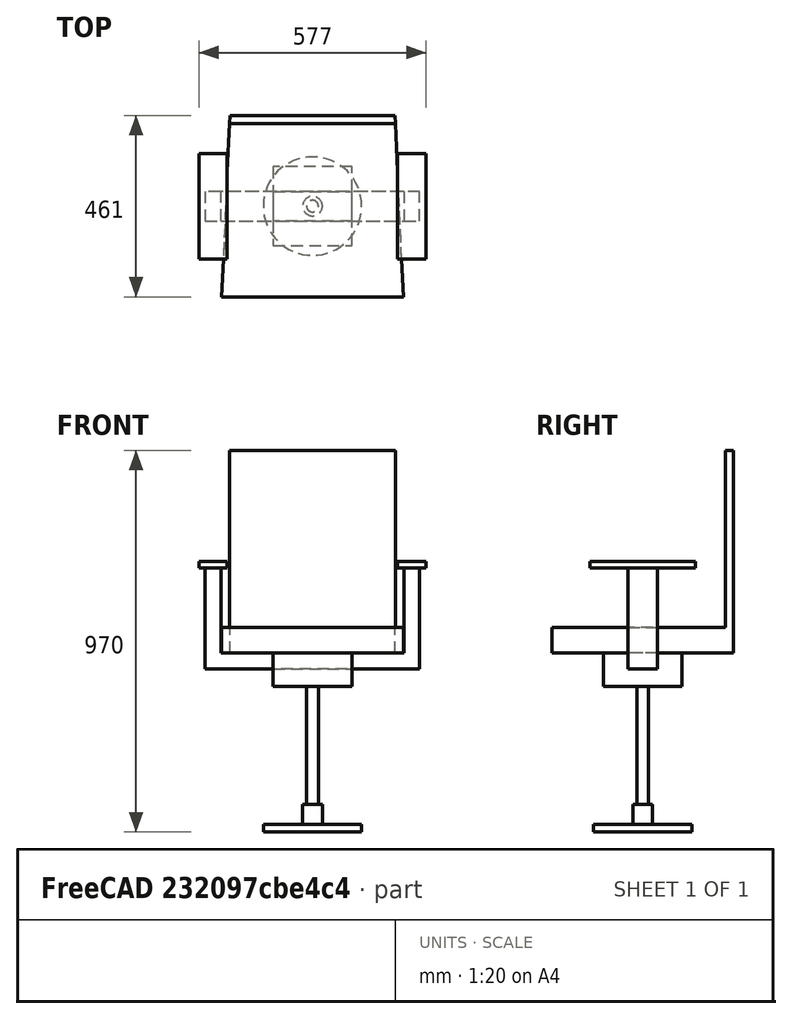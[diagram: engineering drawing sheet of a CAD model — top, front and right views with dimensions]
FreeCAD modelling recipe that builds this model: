
FCSTD DOCUMENT  (FreeCAD 1.0R39109 (Git))
Label: chair02_00504
License: All rights reserved
LicenseURL: https://en.wikipedia.org/wiki/All_rights_reserved
objects: TechDraw::DrawViewDimension×17, Sketcher::SketchObject×10, PartDesign::Pad×10, TechDraw::DrawViewAnnotation×9, PartDesign::Body×5, PartDesign::ShapeBinder×4, TechDraw::DrawSVGTemplate×3, TechDraw::DrawProjGroupItem×3, TechDraw::DrawPage×3, TechDraw::DrawViewSection×3, App::Part×1
note: 90 computed .brp shape members not serialized (recipe doc carries the construction recipe); baked Part::Feature solids carry a one-line shape summary decoded from their .brp

FEATURE [Sketcher::SketchObject] Sketch
  ArcFitTolerance = 1e-06
  AttachmentSupport = -> [XY_Plane]
  FullyConstrained = true
  MakeInternals = false
  MapMode = 5
  sketch-geometry (1):
    g0: Circle CenterX=0 CenterY=0 CenterZ=0 NormalX=0 NormalY=0 NormalZ=1 AngleXU=0 Radius=125
  constraints (2):
    c: Diameter(g0) = 250
    c: Coincident(g0,g-1)
FEATURE [PartDesign::Pad] Pad
  Direction = (0,0,1)
  Length = 20
  Length2 = 10
  Profile = -> Sketch
  ReferenceAxis = -> Sketch [N_Axis]
  Refine = true
  Suppressed = false
  Type = 0
FEATURE [Sketcher::SketchObject] Sketch001
  ArcFitTolerance = 1e-06
  AttachmentSupport = -> [Pad]
  FullyConstrained = true
  MakeInternals = false
  MapMode = 5
  Placement = pos=(0,0,20) rot=(0,0,1;0rad)
  sketch-geometry (1):
    g0: Circle CenterX=0 CenterY=0 CenterZ=0 NormalX=0 NormalY=0 NormalZ=1 AngleXU=0 Radius=25
  constraints (2):
    c: Diameter(g0) = 50
    c: Coincident(g0,g-1)
FEATURE [PartDesign::Pad] Pad001
  BaseFeature = -> Pad
  Direction = (0,0,1)
  Length = 50
  Length2 = 10
  Profile = -> Sketch001
  ReferenceAxis = -> Sketch001 [N_Axis]
  Refine = true
  Suppressed = false
  Type = 0
FEATURE [PartDesign::Body] Body  label="Body1"
  AllowCompound = false
  Group = -> [Sketch,Pad,Sketch001,Pad001]
  Origin = -> Origin
  Tip = -> Pad001
FEATURE [PartDesign::ShapeBinder] CopyPad001  label="Body2_Sketch_P.lane"
  Placement = pos=(0,0,50) rot=(0,0,1;0rad)
  TraceSupport = false
FEATURE [Sketcher::SketchObject] Sketch002
  ArcFitTolerance = 1e-06
  AttachmentSupport = -> [CopyPad001]
  FullyConstrained = true
  MakeInternals = false
  MapMode = 5
  Placement = pos=(0,0,70) rot=(0,0,1;0rad)
  sketch-geometry (1):
    g0: Circle CenterX=0 CenterY=0 CenterZ=0 NormalX=0 NormalY=0 NormalZ=1 AngleXU=0 Radius=15
  constraints (2):
    c: Diameter(g0) = 30
    c: Coincident(g0,g-1)
FEATURE [PartDesign::Pad] Pad002
  Direction = (0,0,1)
  Length = 300
  Length2 = 10
  Placement = pos=(0,0,50) rot=(0,0,1;0rad)
  Profile = -> Sketch002
  ReferenceAxis = -> Sketch002 [N_Axis]
  Refine = true
  Suppressed = false
  Type = 0
FEATURE [PartDesign::Body] Body001  label="Body2"
  AllowCompound = false
  Group = -> [CopyPad001,Sketch002,Pad002]
  Origin = -> Origin001
  Tip = -> Pad002
FEATURE [PartDesign::ShapeBinder] CopyPad002  label="Body3_Sketch_Plane"
  Placement = pos=(0,0,300) rot=(0,0,1;0rad)
  TraceSupport = false
FEATURE [Sketcher::SketchObject] Sketch003
  ArcFitTolerance = 1e-06
  AttachmentSupport = -> [CopyPad002]
  FullyConstrained = true
  MakeInternals = false
  MapMode = 5
  Placement = pos=(0,0,370) rot=(0,0,1;0rad)
  sketch-geometry (5):
    g0: LineSegment StartX=-100 StartY=-100 StartZ=0 EndX=100 EndY=-100 EndZ=0
    g1: LineSegment StartX=100 StartY=-100 StartZ=0 EndX=100 EndY=100 EndZ=0
    g2: LineSegment StartX=100 StartY=100 StartZ=0 EndX=-100 EndY=100 EndZ=0
    g3: LineSegment StartX=-100 StartY=100 StartZ=0 EndX=-100 EndY=-100 EndZ=0
    g4: GeomPoint [constr] X=0 Y=0 Z=0
  constraints (12):
    c: Coincident(g0,g1)
    c: Coincident(g1,g2)
    c: Coincident(g2,g3)
    c: Coincident(g3,g0)
    c: Horizontal(g0)
    c: Horizontal(g2)
    c: Vertical(g1)
    c: Vertical(g3)
    c: Symmetric(g2,g0,g4)
    c: Distance(g1,g3) = 200
    c: Distance(g0,g2) = 200
    c: Coincident(g4,g-1)
FEATURE [PartDesign::Pad] Pad003
  Direction = (0,0,1)
  Length = 45
  Length2 = 10
  Placement = pos=(0,0,300) rot=(0,0,1;0rad)
  Profile = -> Sketch003
  ReferenceAxis = -> Sketch003 [N_Axis]
  Refine = true
  Suppressed = false
  Type = 0
FEATURE [PartDesign::ShapeBinder] CopyPad003  label="Body4_Sketch_Plane"
  Placement = pos=(0,0,45) rot=(0,0,1;0rad)
  TraceSupport = false
FEATURE [Sketcher::SketchObject] Sketch004
  ArcFitTolerance = 1e-06
  AttachmentSupport = -> [CopyPad003]
  FullyConstrained = true
  MakeInternals = false
  MapMode = 5
  Placement = pos=(0,0,415) rot=(0,0,1;0rad)
  sketch-geometry (5):
    g0: LineSegment StartX=-272.5 StartY=-37.5 StartZ=0 EndX=272.5 EndY=-37.5 EndZ=0
    g1: LineSegment StartX=272.5 StartY=-37.5 StartZ=0 EndX=272.5 EndY=37.5 EndZ=0
    g2: LineSegment StartX=272.5 StartY=37.5 StartZ=0 EndX=-272.5 EndY=37.5 EndZ=0
    g3: LineSegment StartX=-272.5 StartY=37.5 StartZ=0 EndX=-272.5 EndY=-37.5 EndZ=0
    g4: GeomPoint [constr] X=0 Y=0 Z=0
  constraints (12):
    c: Coincident(g0,g1)
    c: Coincident(g1,g2)
    c: Coincident(g2,g3)
    c: Coincident(g3,g0)
    c: Horizontal(g0)
    c: Horizontal(g2)
    c: Vertical(g1)
    c: Vertical(g3)
    c: Symmetric(g2,g0,g4)
    c: Distance(g1,g3) = 545
    c: Distance(g0,g2) = 75
    c: Coincident(g4,g-1)
FEATURE [PartDesign::Pad] Pad004
  Direction = (0,0,1)
  Length = 40
  Length2 = 10
  Placement = pos=(0,0,45) rot=(0,0,1;0rad)
  Profile = -> Sketch004
  ReferenceAxis = -> Sketch004 [N_Axis]
  Refine = true
  Suppressed = false
  Type = 0
FEATURE [Sketcher::SketchObject] Sketch005
  ArcFitTolerance = 1e-06
  AttachmentSupport = -> [Pad004]
  ExternalGeometry = -> [Pad004]
  FullyConstrained = true
  MakeInternals = false
  MapMode = 5
  Placement = pos=(0,0,455) rot=(0,0,1;0rad)
  sketch-geometry (8):
    g0: LineSegment StartX=-272.5 StartY=37.5 StartZ=0 EndX=-272.5 EndY=-37.5 EndZ=0
    g1: LineSegment StartX=-272.5 StartY=-37.5 StartZ=0 EndX=-232.5 EndY=-37.5 EndZ=0
    g2: LineSegment StartX=-232.5 StartY=-37.5 StartZ=0 EndX=-232.5 EndY=37.5 EndZ=0
    g3: LineSegment StartX=-232.5 StartY=37.5 StartZ=0 EndX=-272.5 EndY=37.5 EndZ=0
    g4: LineSegment StartX=272.5 StartY=37.5 StartZ=0 EndX=232.5 EndY=37.5 EndZ=0
    g5: LineSegment StartX=232.5 StartY=37.5 StartZ=0 EndX=232.5 EndY=-37.5 EndZ=0
    g6: LineSegment StartX=232.5 StartY=-37.5 StartZ=0 EndX=272.5 EndY=-37.5 EndZ=0
    g7: LineSegment StartX=272.5 StartY=-37.5 StartZ=0 EndX=272.5 EndY=37.5 EndZ=0
  constraints (22):
    c: Coincident(g0,g1)
    c: Coincident(g1,g2)
    c: Coincident(g2,g3)
    c: Coincident(g3,g0)
    c: Vertical(g0)
    c: Vertical(g2)
    c: Horizontal(g1)
    c: Horizontal(g3)
    c: Coincident(g0,g-3)
    c: PointOnObject(g1,g-4)
    c: DistanceX(g3,g3) = 40
    c: Coincident(g4,g5)
    c: Coincident(g5,g6)
    c: Coincident(g6,g7)
    c: Coincident(g7,g4)
    c: Horizontal(g4)
    c: Horizontal(g6)
    c: Vertical(g5)
    c: Vertical(g7)
    c: Coincident(g4,g-3)
    c: PointOnObject(g5,g-4)
    c: Equal(g4,g3)
FEATURE [PartDesign::Pad] Pad005
  BaseFeature = -> Pad004
  Direction = (0,0,1)
  Length = 216
  Length2 = 10
  Placement = pos=(0,0,45) rot=(0,0,1;0rad)
  Profile = -> Sketch005
  ReferenceAxis = -> Sketch005 [N_Axis]
  Refine = true
  Suppressed = false
  Type = 0
FEATURE [Sketcher::SketchObject] Sketch006
  ArcFitTolerance = 1e-06
  AttachmentSupport = -> [Pad005]
  ExternalGeometry = -> [Pad005]
  FullyConstrained = true
  MakeInternals = false
  MapMode = 5
  Placement = pos=(0,0,671) rot=(0,0,1;0rad)
  sketch-geometry (16):
    g0: LineSegment StartX=-288.5 StartY=134 StartZ=0 EndX=-288.5 EndY=-134 EndZ=0
    g1: LineSegment StartX=-288.5 StartY=-134 StartZ=0 EndX=-216.5 EndY=-134 EndZ=0
    g2: LineSegment StartX=-216.5 StartY=-134 StartZ=0 EndX=-216.5 EndY=134 EndZ=0
    g3: LineSegment StartX=-216.5 StartY=134 StartZ=0 EndX=-288.5 EndY=134 EndZ=0
    g4: LineSegment StartX=216.5 StartY=134 StartZ=0 EndX=216.5 EndY=-134 EndZ=0
    g5: LineSegment StartX=216.5 StartY=-134 StartZ=0 EndX=288.5 EndY=-134 EndZ=0
    g6: LineSegment StartX=288.5 StartY=-134 StartZ=0 EndX=288.5 EndY=134 EndZ=0
    g7: LineSegment StartX=288.5 StartY=134 StartZ=0 EndX=216.5 EndY=134 EndZ=0
    g8: LineSegment [constr] StartX=-272.5 StartY=37.5 StartZ=0 EndX=-232.5 EndY=-37.5 EndZ=0
    g9: LineSegment [constr] StartX=-252.5 StartY=0 StartZ=0 EndX=-272.5 EndY=-37.5 EndZ=0
    g10: LineSegment [constr] StartX=232.5 StartY=37.5 StartZ=0 EndX=272.5 EndY=-37.5 EndZ=0
    g11: LineSegment [constr] StartX=272.5 StartY=37.5 StartZ=0 EndX=252.5 EndY=0 EndZ=0
    g12: LineSegment [constr] StartX=-216.5 StartY=134 StartZ=0 EndX=-288.5 EndY=-134 EndZ=0
    g13: LineSegment [constr] StartX=-288.5 StartY=134 StartZ=0 EndX=-252.5 EndY=0 EndZ=0
    g14: LineSegment [constr] StartX=216.5 StartY=134 StartZ=0 EndX=288.5 EndY=-134 EndZ=0
    g15: LineSegment [constr] StartX=288.5 StartY=134 StartZ=0 EndX=252.5 EndY=0 EndZ=0
  constraints (38):
    c: Coincident(g0,g1)
    c: Coincident(g1,g2)
    c: Coincident(g2,g3)
    c: Coincident(g3,g0)
    c: Vertical(g0)
    c: Vertical(g2)
    c: Horizontal(g1)
    c: Horizontal(g3)
    c: Coincident(g4,g5)
    c: Coincident(g5,g6)
    c: Coincident(g6,g7)
    c: Coincident(g7,g4)
    c: Vertical(g4)
    c: Vertical(g6)
    c: Horizontal(g5)
    c: Horizontal(g7)
    c: Equal(g7,g3)
    c: Equal(g2,g4)
    c: DistanceX(g3,g3) = 72
    c: Coincident(g8,g-4)
    c: Coincident(g8,g-3)
    c: Coincident(g9,g-4)
    c: Coincident(g10,g-5)
    c: Coincident(g10,g-6)
    c: Coincident(g11,g-6)
    c: Symmetric(g10,g10,g11)
    c: Symmetric(g8,g8,g9)
    c: Coincident(g12,g2)
    c: Coincident(g12,g0)
    c: Coincident(g13,g0)
    c: Symmetric(g12,g12,g13)
    c: Coincident(g9,g13)
    c: Coincident(g14,g4)
    c: Coincident(g14,g5)
    c: Coincident(g15,g6)
    c: Symmetric(g14,g14,g15)
    c: Coincident(g15,g11)
    c: DistanceY(g2,g2) = 268
FEATURE [PartDesign::Pad] Pad006
  BaseFeature = -> Pad005
  Direction = (0,0,1)
  Length = 17
  Length2 = 10
  Placement = pos=(0,0,45) rot=(0,0,1;0rad)
  Profile = -> Sketch006
  ReferenceAxis = -> Sketch006 [N_Axis]
  Refine = true
  Suppressed = false
  Type = 0
FEATURE [PartDesign::Body] Body003  label="Body4"
  AllowCompound = false
  Group = -> [CopyPad003,Sketch004,Pad004,Sketch005,Pad005,Sketch006,Pad006]
  Origin = -> Origin003
  Tip = -> Pad006
FEATURE [PartDesign::ShapeBinder] CopyPad006  label="Body5_Sketch_Plane"
  Placement = pos=(0,0,45) rot=(0,0,1;0rad)
  TraceSupport = false
FEATURE [Sketcher::SketchObject] Sketch009
  ArcFitTolerance = 1e-06
  AttachmentSupport = -> [Pad003]
  ExternalGeometry = -> [Pad003]
  FullyConstrained = true
  MakeInternals = false
  MapMode = 5
  Placement = pos=(0,0,415) rot=(0,0,1;0rad)
  sketch-geometry (8):
    g0: LineSegment StartX=-100 StartY=100 StartZ=0 EndX=-100 EndY=37.5 EndZ=0
    g1: LineSegment StartX=-100 StartY=37.5 StartZ=0 EndX=100 EndY=37.5 EndZ=0
    g2: LineSegment StartX=100 StartY=37.5 StartZ=0 EndX=100 EndY=100 EndZ=0
    g3: LineSegment StartX=100 StartY=100 StartZ=0 EndX=-100 EndY=100 EndZ=0
    g4: LineSegment StartX=100 StartY=-100 StartZ=0 EndX=100 EndY=-37.5 EndZ=0
    g5: LineSegment StartX=100 StartY=-37.5 StartZ=0 EndX=-100 EndY=-37.5 EndZ=0
    g6: LineSegment StartX=-100 StartY=-37.5 StartZ=0 EndX=-100 EndY=-100 EndZ=0
    g7: LineSegment StartX=-100 StartY=-100 StartZ=0 EndX=100 EndY=-100 EndZ=0
  constraints (21):
    c: Coincident(g0,g1)
    c: Coincident(g1,g2)
    c: Coincident(g2,g3)
    c: Coincident(g3,g0)
    c: Vertical(g0)
    c: Vertical(g2)
    c: Horizontal(g1)
    c: Horizontal(g3)
    c: Coincident(g0,g-3)
    c: PointOnObject(g1,g-4)
    c: Coincident(g4,g5)
    c: Coincident(g5,g6)
    c: Coincident(g6,g7)
    c: Coincident(g7,g4)
    c: Vertical(g6)
    c: Horizontal(g5)
    c: Horizontal(g7)
    c: Coincident(g4,g-4)
    c: PointOnObject(g5,g-3)
    c: DistanceY(g4,g1) = 75
    c: Symmetric(g1,g4,g-1)
FEATURE [PartDesign::Pad] Pad009
  BaseFeature = -> Pad003
  Direction = (0,0,1)
  Length = 40
  Length2 = 10
  Placement = pos=(0,0,300) rot=(0,0,1;0rad)
  Profile = -> Sketch009
  ReferenceAxis = -> Sketch009 [N_Axis]
  Refine = true
  Suppressed = false
  Type = 0
FEATURE [PartDesign::Body] Body002  label="Body3"
  AllowCompound = false
  Group = -> [CopyPad002,Sketch003,Pad003,Sketch009,Pad009]
  Origin = -> Origin002
  Tip = -> Pad009
FEATURE [Sketcher::SketchObject] Sketch007
  ArcFitTolerance = 1e-06
  AttachmentSupport = -> [CopyPad006]
  FullyConstrained = true
  MakeInternals = false
  MapMode = 5
  Placement = pos=(0,0,455) rot=(0,0,1;0rad)
  sketch-geometry (8):
    g0: LineSegment StartX=-210 StartY=230.5 StartZ=0 EndX=-231 EndY=-230.5 EndZ=0
    g1: LineSegment StartX=-231 StartY=-230.5 StartZ=0 EndX=231 EndY=-230.5 EndZ=0
    g2: LineSegment StartX=231 StartY=-230.5 StartZ=0 EndX=210 EndY=230.5 EndZ=0
    g3: LineSegment StartX=210 StartY=230.5 StartZ=0 EndX=-210 EndY=230.5 EndZ=0
    g4: LineSegment [constr] StartX=210 StartY=230.5 StartZ=0 EndX=2.84e-14 EndY=0 EndZ=0
    g5: LineSegment [constr] StartX=2.84e-14 StartY=0 StartZ=0 EndX=-210 EndY=230.5 EndZ=0
    g6: LineSegment [constr] StartX=210 StartY=230.5 StartZ=0 EndX=210 EndY=0 EndZ=0
    g7: LineSegment [constr] StartX=231 StartY=-230.5 StartZ=0 EndX=231 EndY=0 EndZ=0
  constraints (20):
    c: Coincident(g2,g1)
    c: DistanceX(g1,g1) = 462
    c: DistanceX(g3,g3) = 420
    c: Coincident(g1,g0)
    c: Symmetric(g2,g0,g-2)
    c: Coincident(g2,g3)
    c: Coincident(g3,g0)
    c: Coincident(g4,g2)
    c: Coincident(g4,g-1)
    c: Coincident(g5,g4)
    c: Coincident(g5,g0)
    c: DistanceY(g2,g2) = 461
    c: Coincident(g6,g2)
    c: PointOnObject(g6,g-1)
    c: Vertical(g6)
    c: Coincident(g7,g1)
    c: PointOnObject(g7,g-1)
    c: Vertical(g7)
    c: Equal(g7,g6)
    c: Symmetric(g1,g0,g-2)
FEATURE [PartDesign::Pad] Pad007
  Direction = (0,0,1)
  Length = 65
  Length2 = 10
  Placement = pos=(0,0,45) rot=(0,0,1;0rad)
  Profile = -> Sketch007
  ReferenceAxis = -> Sketch007 [N_Axis]
  Refine = true
  Suppressed = false
  Type = 0
FEATURE [Sketcher::SketchObject] Sketch008
  ArcFitTolerance = 1e-06
  AttachmentSupport = -> [Pad007]
  ExternalGeometry = -> [Pad007]
  FullyConstrained = true
  MakeInternals = false
  MapMode = 5
  Placement = pos=(0,0,520) rot=(0,0,1;0rad)
  sketch-geometry (4):
    g0: LineSegment StartX=-210 StartY=230.5 StartZ=0 EndX=210 EndY=230.5 EndZ=0
    g1: LineSegment StartX=-210 StartY=230.5 StartZ=0 EndX=-210.957 EndY=209.5 EndZ=0
    g2: LineSegment StartX=-210.957 StartY=209.5 StartZ=0 EndX=210.957 EndY=209.5 EndZ=0
    g3: LineSegment StartX=210 StartY=230.5 StartZ=0 EndX=210.957 EndY=209.5 EndZ=0
  constraints (10):
    c: Coincident(g0,g-3)
    c: Coincident(g0,g-4)
    c: Coincident(g1,g0)
    c: PointOnObject(g1,g-3)
    c: Coincident(g2,g1)
    c: PointOnObject(g2,g-4)
    c: Horizontal(g2)
    c: Coincident(g3,g0)
    c: Coincident(g3,g2)
    c: DistanceY(g1,g1) = 21
FEATURE [PartDesign::Pad] Pad008
  BaseFeature = -> Pad007
  Direction = (0,0,1)
  Length = 450
  Length2 = 10
  Placement = pos=(0,0,45) rot=(0,0,1;0rad)
  Profile = -> Sketch008
  ReferenceAxis = -> Sketch008 [N_Axis]
  Refine = true
  Suppressed = false
  Type = 0
FEATURE [PartDesign::Body] Body004  label="Body5"
  AllowCompound = false
  Group = -> [CopyPad006,Sketch007,Pad007,Sketch008,Pad008]
  Origin = -> Origin004
  Tip = -> Pad008
FEATURE [App::Part] Part  label="chair02"
  Group = -> [Body,Body001,Body002,Body003,Body004]
  Origin = -> Origin005
FEATURE [TechDraw::DrawSVGTemplate] Template  label="テンプレート"
  Height = 210
  Orientation = 1
  Template = <userpath>/AppData/Local/Programs/FreeCAD 1.0/data/Mod/TechDraw/Templates/A4_Landscape_blank.svg
  Width = 297
FEATURE [TechDraw::DrawProjGroupItem] View
  CoarseView = false
  Direction = (0,0,1)
  Focus = 100
  HardHidden = true
  IsoCount = 0
  IsoHidden = false
  IsoVisible = false
  LockPosition = false
  Perspective = false
  Rotation = 0
  RotationVector = (1,0,0)
  Scale = 0.333333
  ScaleType = 2
  ScrubCount = 1
  SeamHidden = false
  SeamVisible = false
  SmoothHidden = false
  SmoothVisible = true
  Source = -> [Part]
  Type = 0
  X = 131.425
  XDirection = (1,0,0)
  Y = 107.897
FEATURE [TechDraw::DrawViewDimension] Dimension  label="寸法"
  AngleOverride = false
  Arbitrary = false
  ArbitraryTolerances = false
  BoxCorners = (2) [(-96.1666,-76.8333,0),(96.1666,76.8333,0)]
  EqualTolerance = true
  ExtensionAngle = 0
  FormatSpec = %.2w
  FormatSpecOverTolerance = %+.2w
  FormatSpecUnderTolerance = %+.2w
  Inverted = false
  LineAngle = 0
  LockPosition = false
  MeasureType = 1
  OverTolerance = 0
  References2D = -> [View]
  Rotation = 0
  Scale = 0.2
  ScaleType = 2
  TheoreticalExact = false
  Type = 1
  UnderTolerance = 0
  X = 0
  Y = 93.9298
FEATURE [TechDraw::DrawViewDimension] Dimension001  label="寸法001"
  AngleOverride = false
  Arbitrary = false
  ArbitraryTolerances = false
  BoxCorners = (2) [(-96.1666,-76.8333,0),(96.1666,76.8333,0)]
  EqualTolerance = true
  ExtensionAngle = 0
  FormatSpec = %.2w
  FormatSpecOverTolerance = %+.2w
  FormatSpecUnderTolerance = %+.2w
  Inverted = false
  LineAngle = 0
  LockPosition = false
  MeasureType = 1
  OverTolerance = 0
  References2D = -> [View]
  Rotation = 0
  Scale = 0.2
  ScaleType = 2
  TheoreticalExact = false
  Type = 2
  UnderTolerance = 0
  X = 135.701
  Y = 0
FEATURE [TechDraw::DrawViewDimension] Dimension002  label="寸法002"
  AngleOverride = false
  Arbitrary = false
  ArbitraryTolerances = false
  BoxCorners = (2) [(-96.1666,-76.8333,0),(96.1666,76.8333,0)]
  EqualTolerance = true
  ExtensionAngle = 0
  FormatSpec = %.2w
  FormatSpecOverTolerance = %+.2w
  FormatSpecUnderTolerance = %+.2w
  Inverted = false
  LineAngle = 0
  LockPosition = false
  MeasureType = 1
  OverTolerance = 0
  References2D = -> [View]
  Rotation = 0
  Scale = 0.2
  ScaleType = 2
  TheoreticalExact = false
  Type = 2
  UnderTolerance = 0
  X = 113.57
  Y = 61.6706
FEATURE [TechDraw::DrawViewDimension] Dimension003  label="寸法003"
  AngleOverride = false
  Arbitrary = false
  ArbitraryTolerances = false
  BoxCorners = (2) [(-96.1666,-76.8333,0),(96.1666,76.8333,0)]
  EqualTolerance = true
  ExtensionAngle = 0
  FormatSpec = %.2w
  FormatSpecOverTolerance = %+.2w
  FormatSpecUnderTolerance = %+.2w
  Inverted = false
  LineAngle = 0
  LockPosition = false
  MeasureType = 1
  OverTolerance = 0
  References2D = -> [View]
  Rotation = 0
  Scale = 0.2
  ScaleType = 2
  TheoreticalExact = false
  Type = 2
  UnderTolerance = 0
  X = 125.233
  Y = 0.063601
FEATURE [TechDraw::DrawViewDimension] Dimension006  label="寸法006"
  AngleOverride = false
  Arbitrary = false
  ArbitraryTolerances = false
  BoxCorners = (2) [(-96.1666,-76.8333,0),(96.1666,76.8333,0)]
  EqualTolerance = true
  ExtensionAngle = 0
  FormatSpec = %.2w
  FormatSpecOverTolerance = %+.2w
  FormatSpecUnderTolerance = %+.2w
  Inverted = false
  LineAngle = 0
  LockPosition = false
  MeasureType = 1
  OverTolerance = 0
  References2D = -> [View]
  Rotation = 0
  Scale = 0.2
  ScaleType = 2
  TheoreticalExact = false
  Type = 1
  UnderTolerance = 0
  X = 0
  Y = -83.8244
FEATURE [TechDraw::DrawPage] Page  label="用紙"
  KeepUpdated = true
  NextBalloonIndex = 1
  ProjectionType = 0
  Template = -> Template
  Views = -> [View,Dimension,Dimension001,Dimension002,Dimension003,Dimension006]
FEATURE [TechDraw::DrawSVGTemplate] Template001  label="テンプレート001"
  Height = 210
  Orientation = 1
  Template = <userpath>/AppData/Local/Programs/FreeCAD 1.0/data/Mod/TechDraw/Templates/A4_Landscape_blank.svg
  Width = 297
FEATURE [TechDraw::DrawSVGTemplate] Template002  label="テンプレート002"
  Height = 210
  Orientation = 1
  Template = <userpath>/AppData/Local/Programs/FreeCAD 1.0/data/Mod/TechDraw/Templates/A4_Landscape_blank.svg
  Width = 297
FEATURE [TechDraw::DrawProjGroupItem] View001
  CoarseView = false
  Direction = (0,-1,0)
  Focus = 100
  HardHidden = true
  IsoCount = 0
  IsoHidden = false
  IsoVisible = false
  LockPosition = false
  Perspective = false
  Rotation = 0
  RotationVector = (1,0,0)
  Scale = 0.2
  ScaleType = 2
  ScrubCount = 1
  SeamHidden = false
  SeamVisible = false
  SmoothHidden = false
  SmoothVisible = true
  Source = -> [Part]
  Type = 0
  X = 72.2264
  XDirection = (1,0,0)
  Y = 108.632
FEATURE [TechDraw::DrawViewSection] SectionView  label="セクション  - "
  BaseView = -> View001
  CoarseView = false
  CutSurfaceDisplay = 2
  Direction = (1e-16,0,1)
  FileGeomPattern = <userpath>\AppData\Local\Programs\FreeCAD 1.0\data\Mod/TechDraw/PAT/FCPAT.pat
  FileHatchPattern = <userpath>\AppData\Local\Programs\FreeCAD 1.0\data\Mod/TechDraw/Patterns/simple.svg
  Focus = 100
  FuseBeforeCut = false
  HardHidden = true
  HatchOffset = (0,0,0)
  HatchRotation = 0
  HatchScale = 1
  IsoCount = 0
  IsoHidden = false
  IsoVisible = false
  LockPosition = false
  NameGeomPattern = Diamond
  Perspective = false
  Rotation = 0
  Scale = 0.15
  ScaleType = 2
  ScrubCount = 1
  SeamHidden = false
  SeamVisible = false
  SectionDirection = 4
  SectionLineStretch = 1
  SectionNormal = (1e-16,0,1)
  SectionOrigin = (0,0,581)
  SmoothHidden = false
  SmoothVisible = true
  Source = -> [Part]
  TrimAfterCut = false
  UsePreviousCut = false
  X = 215.858
  XDirection = (1,0,-1e-16)
  Y = 166.085
FEATURE [TechDraw::DrawViewSection] SectionView001  label="セクション001  - "
  BaseView = -> View001
  CoarseView = false
  CutSurfaceDisplay = 2
  Direction = (1e-16,0,1)
  FileGeomPattern = <userpath>\AppData\Local\Programs\FreeCAD 1.0\data\Mod/TechDraw/PAT/FCPAT.pat
  FileHatchPattern = <userpath>\AppData\Local\Programs\FreeCAD 1.0\data\Mod/TechDraw/Patterns/simple.svg
  Focus = 100
  FuseBeforeCut = false
  HardHidden = true
  HatchOffset = (0,0,0)
  HatchRotation = 0
  HatchScale = 1
  IsoCount = 0
  IsoHidden = false
  IsoVisible = false
  LockPosition = false
  NameGeomPattern = Diamond
  Perspective = false
  Rotation = 0
  Scale = 0.15
  ScaleType = 2
  ScrubCount = 1
  SeamHidden = false
  SeamVisible = false
  SectionDirection = 4
  SectionLineStretch = 1
  SectionNormal = (1e-16,0,1)
  SectionOrigin = (0,0,437)
  SmoothHidden = false
  SmoothVisible = true
  Source = -> [Part]
  TrimAfterCut = false
  UsePreviousCut = false
  X = 215.086
  XDirection = (1,0,-1e-16)
  Y = 92.3168
FEATURE [TechDraw::DrawViewSection] SectionView002  label="セクション002  - "
  BaseView = -> View001
  CoarseView = false
  CutSurfaceDisplay = 2
  Direction = (1e-16,0,1)
  FileGeomPattern = <userpath>\AppData\Local\Programs\FreeCAD 1.0\data\Mod/TechDraw/PAT/FCPAT.pat
  FileHatchPattern = <userpath>\AppData\Local\Programs\FreeCAD 1.0\data\Mod/TechDraw/Patterns/simple.svg
  Focus = 100
  FuseBeforeCut = false
  HardHidden = true
  HatchOffset = (0,0,0)
  HatchRotation = 0
  HatchScale = 1
  IsoCount = 0
  IsoHidden = false
  IsoVisible = false
  LockPosition = false
  NameGeomPattern = Diamond
  Perspective = false
  Rotation = 0
  Scale = 0.15
  ScaleType = 2
  ScrubCount = 1
  SeamHidden = false
  SeamVisible = false
  SectionDirection = 4
  SectionLineStretch = 1
  SectionNormal = (1e-16,0,1)
  SectionOrigin = (0,0,200)
  SmoothHidden = false
  SmoothVisible = true
  Source = -> [Part]
  TrimAfterCut = false
  UsePreviousCut = false
  X = 214.868
  XDirection = (1,0,-1e-16)
  Y = 24.434
FEATURE [TechDraw::DrawViewDimension] Dimension007  label="寸法007"
  AngleOverride = false
  Arbitrary = false
  ArbitraryTolerances = false
  BoxCorners = (2) [(-40.875,-34.575,0),(40.875,34.575,0)]
  EqualTolerance = true
  ExtensionAngle = 0
  FormatSpec = %.2w
  FormatSpecOverTolerance = %+.2w
  FormatSpecUnderTolerance = %+.2w
  Inverted = false
  LineAngle = 0
  LockPosition = false
  MeasureType = 1
  OverTolerance = 0
  References2D = -> [SectionView]
  Rotation = 0
  Scale = 0.2
  ScaleType = 2
  TheoreticalExact = false
  Type = 1
  UnderTolerance = 0
  X = 48.3858
  Y = 24.3952
FEATURE [TechDraw::DrawViewDimension] Dimension008  label="寸法008"
  AngleOverride = false
  Arbitrary = false
  ArbitraryTolerances = false
  BoxCorners = (2) [(-40.875,-34.575,0),(40.875,34.575,0)]
  EqualTolerance = true
  ExtensionAngle = 0
  FormatSpec = %.2w
  FormatSpecOverTolerance = %+.2w
  FormatSpecUnderTolerance = %+.2w
  Inverted = false
  LineAngle = 0
  LockPosition = false
  MeasureType = 1
  OverTolerance = 0
  References2D = -> [SectionView]
  Rotation = 0
  Scale = 0.2
  ScaleType = 2
  TheoreticalExact = false
  Type = 2
  UnderTolerance = 0
  X = 59.3049
  Y = -11.5187
FEATURE [TechDraw::DrawViewDimension] Dimension009  label="寸法009"
  AngleOverride = false
  Arbitrary = false
  ArbitraryTolerances = false
  BoxCorners = (2) [(-40.875,-18.75,0),(40.875,18.75,0)]
  EqualTolerance = true
  ExtensionAngle = 0
  FormatSpec = %.2w
  FormatSpecOverTolerance = %+.2w
  FormatSpecUnderTolerance = %+.2w
  Inverted = false
  LineAngle = 0
  LockPosition = false
  MeasureType = 1
  OverTolerance = 0
  References2D = -> [SectionView001]
  Rotation = 0
  Scale = 0.2
  ScaleType = 2
  TheoreticalExact = false
  Type = 1
  UnderTolerance = 0
  X = 0
  Y = -24.3529
FEATURE [TechDraw::DrawViewDimension] Dimension010  label="寸法010"
  AngleOverride = false
  Arbitrary = false
  ArbitraryTolerances = false
  BoxCorners = (2) [(-40.875,-18.75,0),(40.875,18.75,0)]
  EqualTolerance = true
  ExtensionAngle = 0
  FormatSpec = %.2w
  FormatSpecOverTolerance = %+.2w
  FormatSpecUnderTolerance = %+.2w
  Inverted = false
  LineAngle = 0
  LockPosition = false
  MeasureType = 1
  OverTolerance = 0
  References2D = -> [SectionView001]
  Rotation = 0
  Scale = 0.2
  ScaleType = 2
  TheoreticalExact = false
  Type = 1
  UnderTolerance = 0
  X = -23.2227
  Y = -15.8558
FEATURE [TechDraw::DrawViewDimension] Dimension011  label="寸法011"
  AngleOverride = false
  Arbitrary = false
  ArbitraryTolerances = false
  BoxCorners = (2) [(-40.875,-18.75,0),(40.875,18.75,0)]
  EqualTolerance = true
  ExtensionAngle = 0
  FormatSpec = %.2w
  FormatSpecOverTolerance = %+.2w
  FormatSpecUnderTolerance = %+.2w
  Inverted = false
  LineAngle = 0
  LockPosition = false
  MeasureType = 1
  OverTolerance = 0
  References2D = -> [SectionView001]
  Rotation = 0
  Scale = 0.2
  ScaleType = 2
  TheoreticalExact = false
  Type = 2
  UnderTolerance = 0
  X = 58.5124
  Y = 0
FEATURE [TechDraw::DrawViewDimension] Dimension012  label="寸法012"
  AngleOverride = false
  Arbitrary = false
  ArbitraryTolerances = false
  BoxCorners = (2) [(-40.875,-18.75,0),(40.875,18.75,0)]
  EqualTolerance = true
  ExtensionAngle = 0
  FormatSpec = %.2w
  FormatSpecOverTolerance = %+.2w
  FormatSpecUnderTolerance = %+.2w
  Inverted = false
  LineAngle = 0
  LockPosition = false
  MeasureType = 1
  OverTolerance = 0
  References2D = -> [SectionView001]
  Rotation = 0
  Scale = 0.2
  ScaleType = 2
  TheoreticalExact = false
  Type = 2
  UnderTolerance = 0
  X = 72.3404
  Y = 0
FEATURE [TechDraw::DrawViewDimension] Dimension013  label="寸法013"
  AngleOverride = false
  Arbitrary = false
  ArbitraryTolerances = false
  BoxCorners = (2) [(-18.75,-18.75,0),(18.75,18.75,0)]
  EqualTolerance = true
  ExtensionAngle = 0
  FormatSpec = ⌀%.2w
  FormatSpecOverTolerance = %+.2w
  FormatSpecUnderTolerance = %+.2w
  Inverted = false
  LineAngle = 0
  LockPosition = false
  MeasureType = 1
  OverTolerance = 0
  References2D = -> [SectionView002]
  Rotation = 0
  Scale = 0.2
  ScaleType = 2
  TheoreticalExact = false
  Type = 5
  UnderTolerance = 0
  X = 8.10016
  Y = -8.95927
FEATURE [TechDraw::DrawViewDimension] Dimension014  label="寸法014"
  AngleOverride = false
  Arbitrary = false
  ArbitraryTolerances = false
  BoxCorners = (2) [(-18.75,-18.75,0),(18.75,18.75,0)]
  EqualTolerance = true
  ExtensionAngle = 0
  FormatSpec = ⌀%.2w
  FormatSpecOverTolerance = %+.2w
  FormatSpecUnderTolerance = %+.2w
  Inverted = false
  LineAngle = 0
  LockPosition = false
  MeasureType = 1
  OverTolerance = 0
  References2D = -> [SectionView002]
  Rotation = 0
  Scale = 0.2
  ScaleType = 2
  TheoreticalExact = false
  Type = 5
  UnderTolerance = 0
  X = 10.9229
  Y = 0.736379
FEATURE [TechDraw::DrawViewDimension] Dimension015  label="寸法015"
  AngleOverride = false
  Arbitrary = false
  ArbitraryTolerances = false
  BoxCorners = (2) [(-18.75,-18.75,0),(18.75,18.75,0)]
  EqualTolerance = true
  ExtensionAngle = 0
  FormatSpec = ⌀%.2w
  FormatSpecOverTolerance = %+.2w
  FormatSpecUnderTolerance = %+.2w
  Inverted = false
  LineAngle = 0
  LockPosition = false
  MeasureType = 1
  OverTolerance = 0
  References2D = -> [SectionView002]
  Rotation = 0
  Scale = 0.2
  ScaleType = 2
  TheoreticalExact = false
  Type = 5
  UnderTolerance = 0
  X = 22.705
  Y = 18.6549
FEATURE [TechDraw::DrawViewDimension] Dimension016  label="寸法016"
  AngleOverride = false
  Arbitrary = false
  ArbitraryTolerances = false
  BoxCorners = (2) [(-40.875,-34.575,0),(40.875,34.575,0)]
  EqualTolerance = true
  ExtensionAngle = 0
  FormatSpec = %.2w
  FormatSpecOverTolerance = %+.2w
  FormatSpecUnderTolerance = %+.2w
  Inverted = false
  LineAngle = 0
  LockPosition = false
  MeasureType = 1
  OverTolerance = 0
  References2D = -> [SectionView]
  Rotation = 0
  Scale = 0.2
  ScaleType = 2
  TheoreticalExact = false
  Type = 1
  UnderTolerance = 0
  X = 21.6748
  Y = -21.6209
FEATURE [TechDraw::DrawViewAnnotation] Annotation  label="注釈"
  Font = osifont
  LineSpace = 100
  LockPosition = false
  MaxWidth = -1
  Rotation = 0
  Scale = 0.2
  ScaleType = 2
  Text = A
  TextSize = 5
  TextStyle = 0
  X = 143.937
  Y = 118.99
FEATURE [TechDraw::DrawViewAnnotation] Annotation001  label="注釈001"
  Font = osifont
  LineSpace = 100
  LockPosition = false
  MaxWidth = -1
  Rotation = 0
  Scale = 0.2
  ScaleType = 2
  Text = A
  TextSize = 5
  TextStyle = 0
  X = 9.25009
  Y = 118.99
FEATURE [TechDraw::DrawViewAnnotation] Annotation002  label="注釈002"
  Font = osifont
  LineSpace = 100
  LockPosition = false
  MaxWidth = -1
  Rotation = 0
  Scale = 0.2
  ScaleType = 2
  Text = B
  TextSize = 5
  TextStyle = 0
  X = 9.25009
  Y = 89.4351
FEATURE [TechDraw::DrawViewAnnotation] Annotation003  label="注釈003"
  Font = osifont
  LineSpace = 100
  LockPosition = false
  MaxWidth = -1
  Rotation = 0
  Scale = 0.2
  ScaleType = 2
  Text = B
  TextSize = 5
  TextStyle = 0
  X = 145.458
  Y = 89.1146
FEATURE [TechDraw::DrawViewAnnotation] Annotation004  label="注釈004"
  Font = osifont
  LineSpace = 100
  LockPosition = false
  MaxWidth = -1
  Rotation = 0
  Scale = 0.2
  ScaleType = 2
  Text = C
  TextSize = 5
  TextStyle = 0
  X = 145.458
  Y = 40.7495
FEATURE [TechDraw::DrawViewAnnotation] Annotation005  label="注釈005"
  Font = osifont
  LineSpace = 100
  LockPosition = false
  MaxWidth = -1
  Rotation = 0
  Scale = 0.2
  ScaleType = 2
  Text = C
  TextSize = 5
  TextStyle = 0
  X = 9.25009
  Y = 43.6474
FEATURE [TechDraw::DrawViewAnnotation] Annotation006  label="注釈006"
  Font = osifont
  LineSpace = 100
  LockPosition = false
  MaxWidth = -1
  Rotation = 0
  Scale = 0.2
  ScaleType = 2
  Text = A-A
  TextSize = 5
  TextStyle = 0
  X = 215.858
  Y = 205.891
FEATURE [TechDraw::DrawViewAnnotation] Annotation007  label="注釈007"
  Font = osifont
  LineSpace = 100
  LockPosition = false
  MaxWidth = -1
  Rotation = 0
  Scale = 0.2
  ScaleType = 2
  Text = B-B
  TextSize = 5
  TextStyle = 0
  X = 215.858
  Y = 117.871
FEATURE [TechDraw::DrawViewAnnotation] Annotation008  label="注釈008"
  Font = osifont
  LineSpace = 100
  LockPosition = false
  MaxWidth = -1
  Rotation = 0
  Scale = 0.2
  ScaleType = 2
  Text = C -C
  TextSize = 5
  TextStyle = 0
  X = 215.858
  Y = 48.4539
FEATURE [TechDraw::DrawPage] Page002  label="用紙002"
  KeepUpdated = true
  NextBalloonIndex = 1
  ProjectionType = 0
  Template = -> Template002
  Views = -> [View001,SectionView,SectionView001,SectionView002,Dimension007,Dimension008,Dimension009,Dimension010,Dimension011,Dimension012,Dimension013,Dimension014,Dimension015,Dimension016,Annotation,Annotation001,Annotation002,Annotation003,Annotation004,Annotation005,Annotation006,Annotation007,Annotation008]
FEATURE [TechDraw::DrawProjGroupItem] View002
  CoarseView = false
  Direction = (0,-1,0)
  Focus = 100
  HardHidden = true
  IsoCount = 0
  IsoHidden = false
  IsoVisible = false
  LockPosition = false
  Perspective = false
  Rotation = 0
  RotationVector = (1,0,0)
  Scale = 0.2
  ScaleType = 2
  ScrubCount = 1
  SeamHidden = false
  SeamVisible = false
  SmoothHidden = false
  SmoothVisible = true
  Source = -> [Part]
  Type = 0
  X = 144.274
  XDirection = (1,0,0)
  Y = 104.736
FEATURE [TechDraw::DrawViewDimension] Dimension017  label="寸法017"
  AngleOverride = false
  Arbitrary = false
  ArbitraryTolerances = false
  BoxCorners = (2) [(-48.0834,-80.8335,-1e-07),(48.0834,80.8335,1e-07)]
  EqualTolerance = true
  ExtensionAngle = 0
  FormatSpec = %.2w
  FormatSpecOverTolerance = %+.2w
  FormatSpecUnderTolerance = %+.2w
  Inverted = false
  LineAngle = 0
  LockPosition = false
  MeasureType = 1
  OverTolerance = 0
  References2D = -> [View002]
  Rotation = 0
  Scale = 0.2
  ScaleType = 2
  TheoreticalExact = false
  Type = 2
  UnderTolerance = 0
  X = 71.6242
  Y = 43.3334
FEATURE [TechDraw::DrawViewDimension] Dimension019  label="寸法019"
  AngleOverride = false
  Arbitrary = false
  ArbitraryTolerances = false
  BoxCorners = (2) [(-48.0834,-80.8335,-1e-07),(48.0834,80.8335,1e-07)]
  EqualTolerance = true
  ExtensionAngle = 0
  FormatSpec = %.2w
  FormatSpecOverTolerance = %+.2w
  FormatSpecUnderTolerance = %+.2w
  Inverted = false
  LineAngle = 0
  LockPosition = false
  MeasureType = 1
  OverTolerance = 0
  References2D = -> [View002]
  Rotation = 0
  Scale = 0.2
  ScaleType = 2
  TheoreticalExact = false
  Type = 2
  UnderTolerance = 0
  X = 71.6242
  Y = 0.416668
FEATURE [TechDraw::DrawPage] Page001  label="用紙001"
  KeepUpdated = true
  NextBalloonIndex = 1
  ProjectionType = 0
  Template = -> Template001
  Views = -> [View002,Dimension017,Dimension019]
